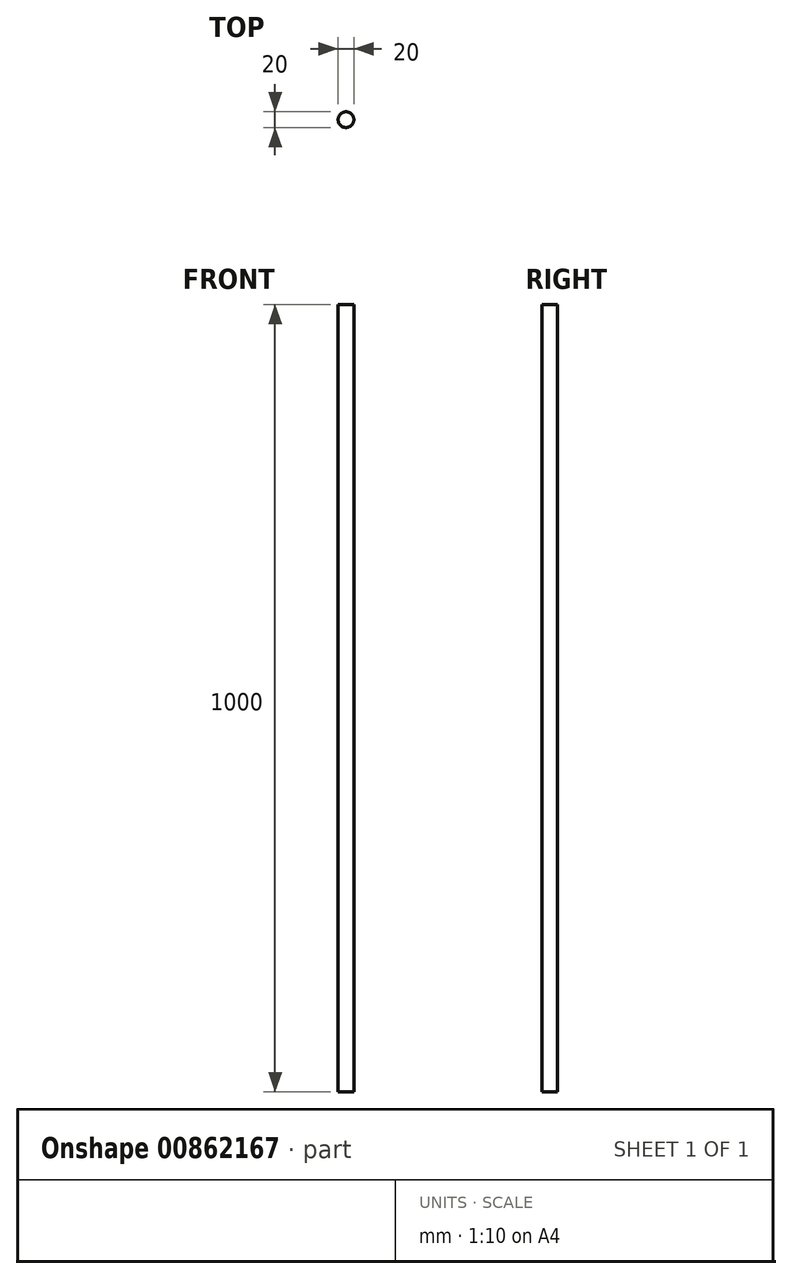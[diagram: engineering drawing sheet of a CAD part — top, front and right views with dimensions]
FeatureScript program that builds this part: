
annotation { "Feature Type Name" : "Feature", "Feature Type Description" : "" }
export const myFeature = defineFeature(function(context is Context, id is Id, definition is map)
    precondition{}
    {
        {
            var Q0;
            Q0=qCreatedBy(makeId("Top.planeOp"),FACE);
            var sketch = newSketch(context, id + "F0", { "sketchPlane" : qUnion([Q0])});
            skCircle(sketch, "E0", {"center": v(0, 0) * mm, "radius": 10 * mm});
            skSolve(sketch);
        }
        {
            var Q0;
            Q0 = qSketchRegion(id + "F0", true);
            extrude(context, id + "F1", {"entities" : qUnion([Q0]), "depth" : 1000 * mm, "offsetDistance" : 25 * mm});
        }
    });
